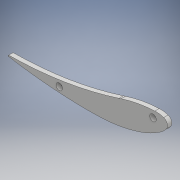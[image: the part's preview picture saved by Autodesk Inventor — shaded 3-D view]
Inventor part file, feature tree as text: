
AUTODESK INVENTOR PART (.ipt)
format: ipt  version: 2018.2 (Build 222227000, 227)  size: 134,656 bytes
history: native  units: mm
features: extrude x2, sketch x2, other x1, projected_geometry x1
ambient origin geometry x8: Origin, YZ Plane, XZ Plane, XY Plane, X Axis, Y Axis, Z Axis, Center Point
bodies: Body1 (feature_tree)
feature tree (6):
  extrude  "押し出し1"  Depth=4.0mm TaperAngle=0.0deg
  extrude  "押し出し2"  Depth=6.0mm
  other  "厚み1"
  sketch  "スケッチ1"
  projected_geometry  "投影ループ1"
  sketch  "スケッチ2"
